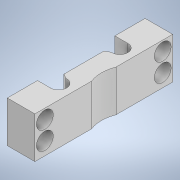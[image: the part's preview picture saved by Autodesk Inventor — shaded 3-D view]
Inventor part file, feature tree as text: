
AUTODESK INVENTOR PART (.ipt)
format: ipt  version: 2020 (Build 240168000, 168)  size: 174,592 bytes
history: native  units: mm
features: extrude x4, sketch x3, other x1
ambient origin geometry x8: Origin, YZ Plane, XZ Plane, XY Plane, X Axis, Y Axis, Z Axis, Center Point
bodies: Body1 (feature_tree)
feature tree (8):
  other  "Bryła1"
  extrude  "Wyciągnięcie proste1"  Depth=1.0mm
  sketch  "Szkic3"
  extrude  "Wyciągnięcie proste2"  Depth=20.0mm
  extrude  "Wyciągnięcie proste3"  Depth=90.0mm
  extrude  "Wyciągnięcie proste4"  Depth=45.0mm
  sketch  "Szkic2"
  sketch  "Szkic4"
